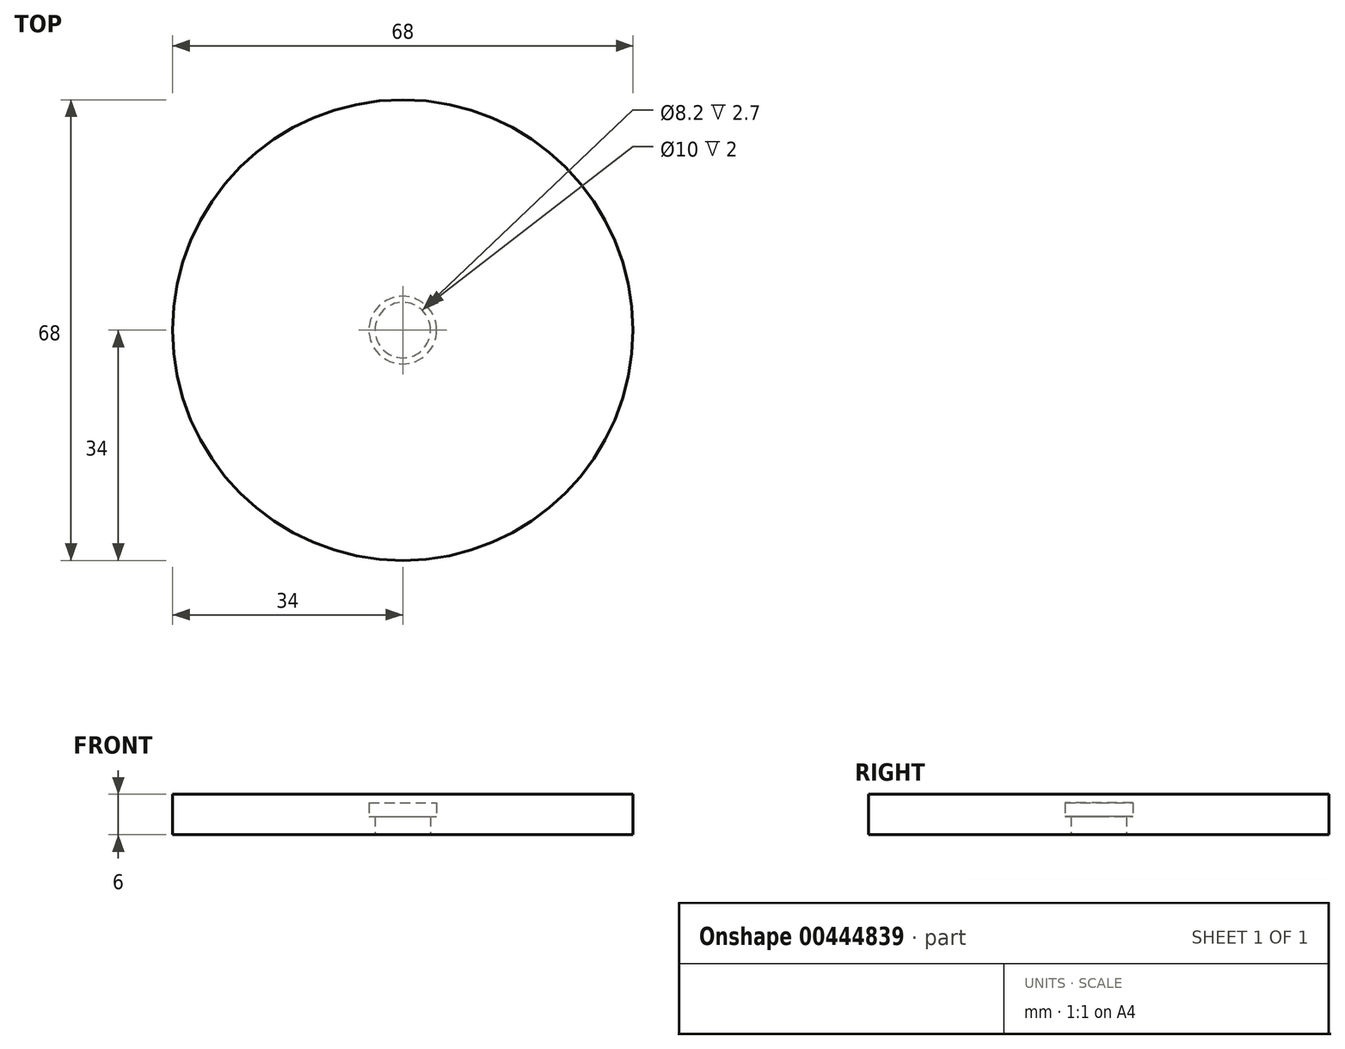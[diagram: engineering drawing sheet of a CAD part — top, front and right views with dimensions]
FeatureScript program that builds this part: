
annotation { "Feature Type Name" : "Feature", "Feature Type Description" : "" }
export const myFeature = defineFeature(function(context is Context, id is Id, definition is map)
    precondition{}
    {
        {
            var Q0;
            Q0=qCreatedBy(makeId("Top.planeOp"),FACE);
            var sketch = newSketch(context, id + "F0", { "sketchPlane" : qUnion([Q0])});
            skCircle(sketch, "E0", {"center": v(0, 0) * mm, "radius": 34 * mm});
            skSolve(sketch);
        }
        {
            var Q0;
            Q0=makeQuery(id+"F0.imprint","IMPRINT",FACE,{"disambiguationData":[TD([[makeQuery(id+"F0.imprint","IMPRINT",EDGE,{"derivedFrom":sQuery(id+"F0.wireOp",EDGE,"E0")}),1.0]])]});
            extrude(context, id + "F1", {"entities" : qUnion([Q0]), "depth" : 6 * mm});
        }
        {
            var Q0;
            Q0=qCreatedBy(makeId("Right.planeOp"),FACE);
            var sketch = newSketch(context, id + "F2", { "sketchPlane" : qUnion([Q0])});
            skLineSegment(sketch, "E1.bottom", {"start": v(4.1, 0) * mm, "end": v(-4.1, 0) * mm});
            skLineSegment(sketch, "E1.top", {"start": v(4.1, 2.7) * mm, "end": v(0, 2.7) * mm});
            skLineSegment(sketch, "E1.left", {"start": v(4.1, 0) * mm, "end": v(4.1, 2.7) * mm});
            skPoint(sketch, "E1.middle", {"position": v(0, 1.35) * mm});
            skLineSegment(sketch, "E2", {"start": v(0, 2.7) * mm, "end": v(0, 0) * mm});
            skPoint(sketch, "E1.right.end.orphan", {"position": v(-4.1, 2.7) * mm});
            skSolve(sketch);
        }
        {
            var Q0;
            Q0 = qSketchRegion(id + "F2", true);
            var Q1;
            Q1=sQuery(id+"F2.wireOp",EDGE,"E2");
            revolve(context, id + "F3", {"operationType" : NewBodyOperationType.REMOVE, "entities" : qUnion([Q0]), "axis" : qUnion([Q1]), "revolveType" : RevolveType.FULL, "oppositeDirection" : true});
        }
        {
            var Q0;
            Q0=makeQuery(id+"F3.boolean.opBoolean","COPY",FACE,{"derivedFrom":makeQuery(id+"F3.opRevolve","SWEPT_FACE",FACE,{"disambiguationData":[OSD([sQuery(id+"F2.wireOp",EDGE,"E1.top")])]})});
            var sketch = newSketch(context, id + "F4", { "sketchPlane" : qUnion([Q0])});
            skCircle(sketch, "E3", {"center": v(0, 0) * mm, "radius": 5 * mm});
            skSolve(sketch);
        }
        {
            var Q0;
            Q0 = qSketchRegion(id + "F4", true);
            extrude(context, id + "F5", {"entities" : qUnion([Q0]), "operationType" : NewBodyOperationType.REMOVE, "oppositeDirection" : true, "depth" : 2 * mm});
        }
    });
